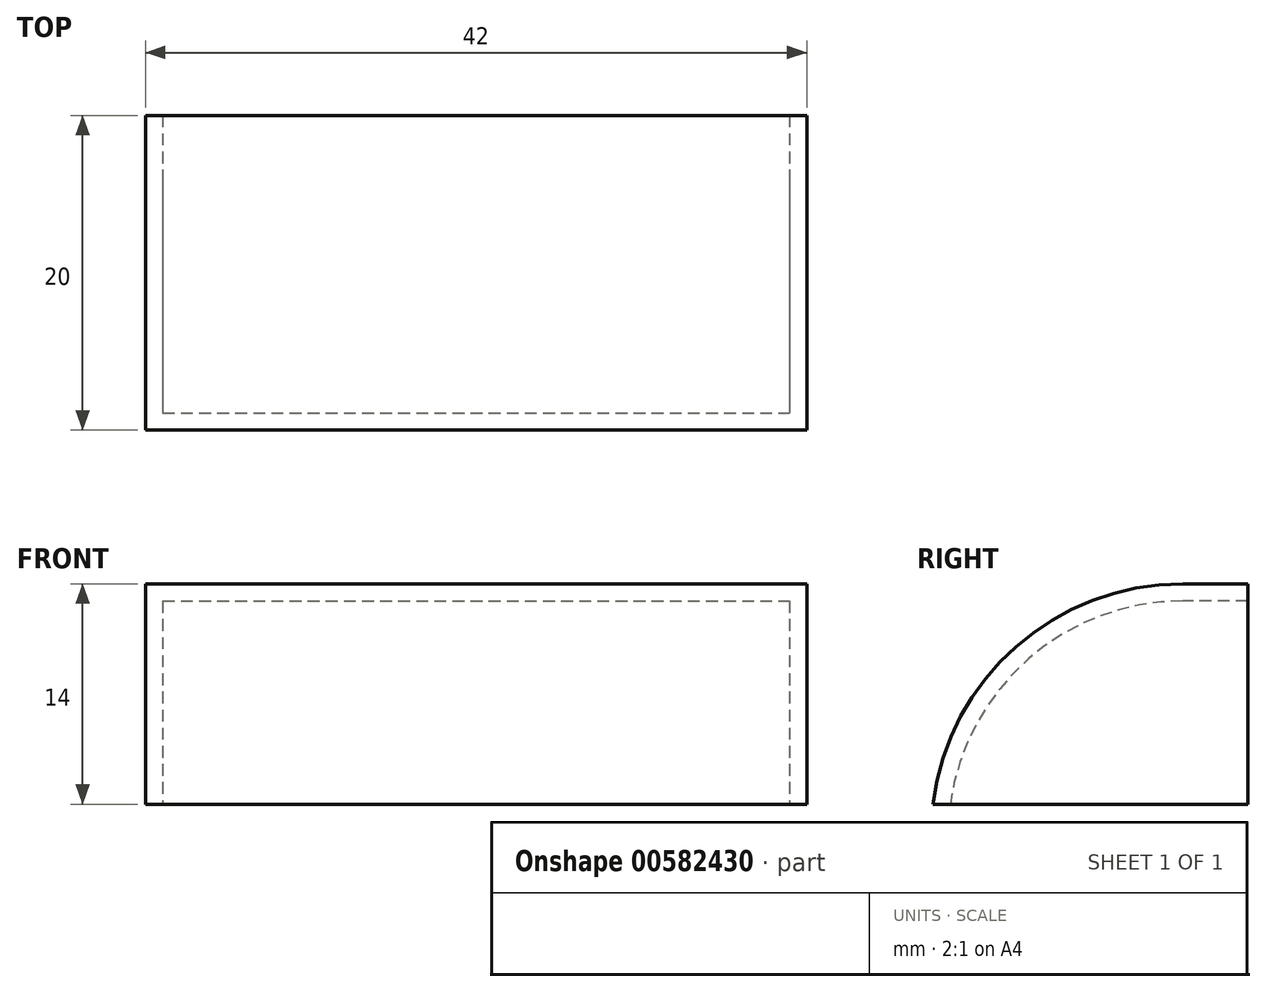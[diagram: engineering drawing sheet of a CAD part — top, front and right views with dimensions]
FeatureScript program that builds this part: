
annotation { "Feature Type Name" : "Feature", "Feature Type Description" : "" }
export const myFeature = defineFeature(function(context is Context, id is Id, definition is map)
    precondition{}
    {
        {
            var Q0;
            Q0=qCreatedBy(makeId("Top.planeOp"),FACE);
            var sketch = newSketch(context, id + "F0", { "sketchPlane" : qUnion([Q0])});
            skLineSegment(sketch, "E0.bottom", {"start": v(-21, 10) * mm, "end": v(21, 10) * mm});
            skLineSegment(sketch, "E0.top", {"start": v(-21, -10) * mm, "end": v(21, -10) * mm});
            skLineSegment(sketch, "E0.left", {"start": v(-21, 10) * mm, "end": v(-21, -10) * mm});
            skLineSegment(sketch, "E0.right", {"start": v(21, 10) * mm, "end": v(21, -10) * mm});
            skSolve(sketch);
        }
        {
            var Q0;
            Q0 = qSketchRegion(id + "F0", true);
            extrude(context, id + "F1", {"entities" : qUnion([Q0]), "depth" : 14 * mm, "offsetDistance" : 25 * mm});
        }
        {
            var Q0;
            Q0=makeQuery(id+"F1.opExtrude","CAP_EDGE",EDGE,{"disambiguationData":[OSD([sQuery(id+"F0.wireOp",EDGE,"E0.top")])],"isStart":false});
            fillet(context, id + "F2", {"entities" : qUnion([Q0]), "radius" : 16 * mm, "tangentPropagation" : true, "allowEdgeOverflow" : false});
        }
        {
            var Q0;
            Q0=makeQuery(id+"F1.opExtrude","SWEPT_FACE",FACE,{"disambiguationData":[OSD([sQuery(id+"F0.wireOp",EDGE,"E0.bottom")])]});
            var Q1;
            Q1=makeQuery(id+"F1.opExtrude","CAP_FACE",FACE,{"disambiguationData":[OSD([sQuery(id+"F0.wireOp",EDGE,"E0.bottom"),sQuery(id+"F0.wireOp",EDGE,"E0.top"),sQuery(id+"F0.wireOp",EDGE,"E0.left"),sQuery(id+"F0.wireOp",EDGE,"E0.right")])],"isStart":true});
            shell(context, id + "F3", {"entities" : qUnion([Q0, Q1]), "thickness" : 1.1 * mm});
        }
    });
